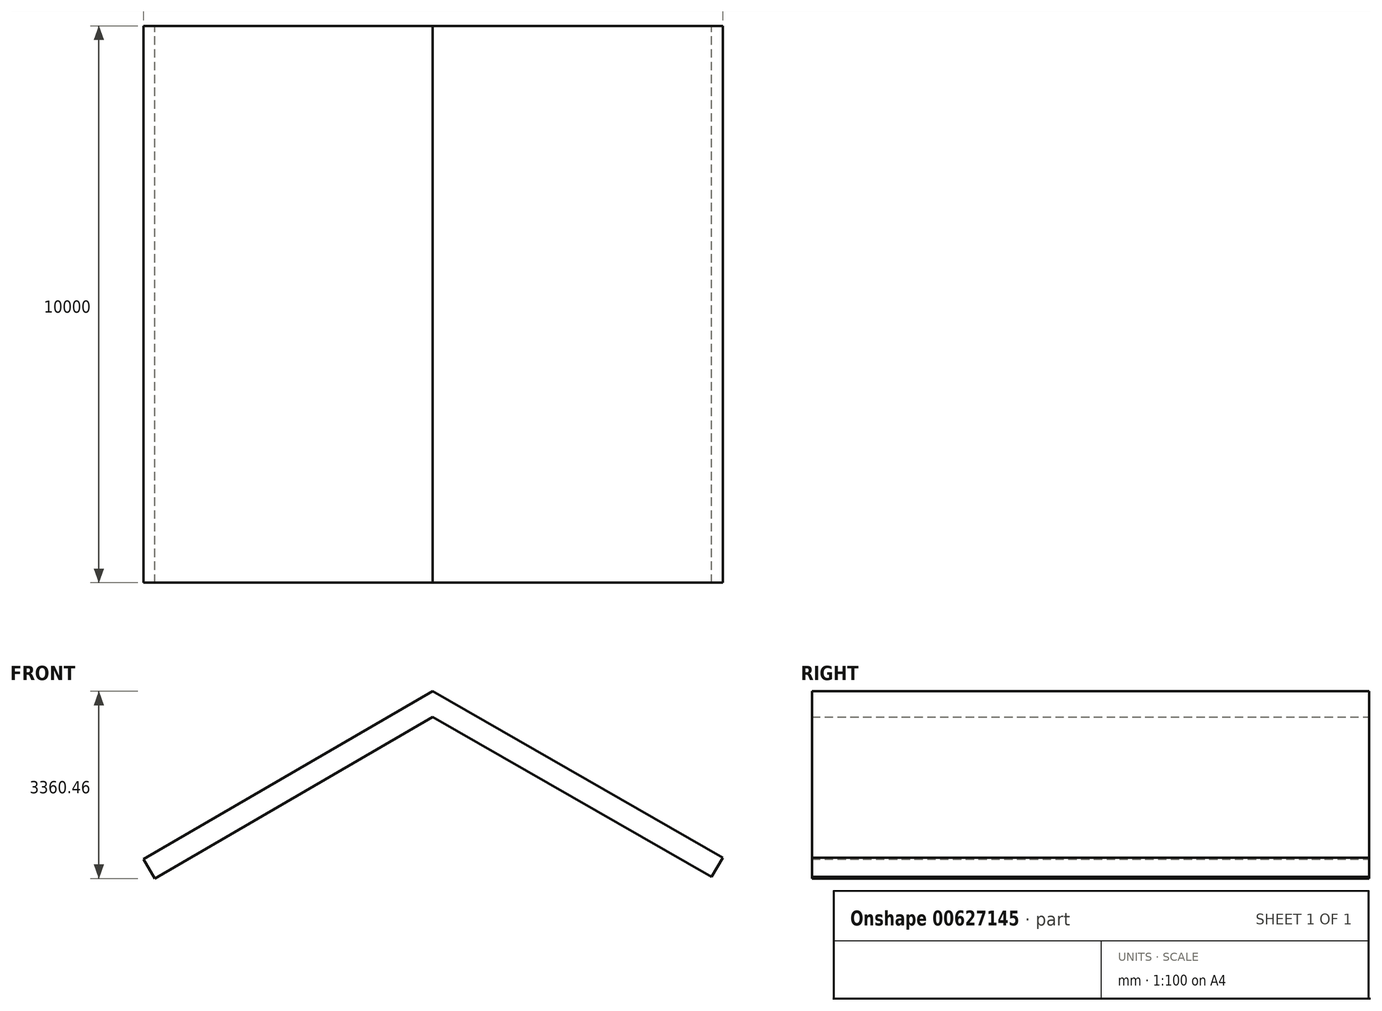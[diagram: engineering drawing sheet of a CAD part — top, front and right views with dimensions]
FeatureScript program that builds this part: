
annotation { "Feature Type Name" : "Feature", "Feature Type Description" : "" }
export const myFeature = defineFeature(function(context is Context, id is Id, definition is map)
    precondition{}
    {
        {
            var Q0;
            Q0=qCreatedBy(makeId("Front.planeOp"),FACE);
            var sketch = newSketch(context, id + "F0", { "sketchPlane" : qUnion([Q0])});
            skLineSegment(sketch, "E0", {"start": v(-86.15, -17.85) * mm, "end": v(5101.54, 2996.77) * mm});
            skLineSegment(sketch, "E1", {"start": v(5101.54, 2996.77) * mm, "end": v(10306.11, 11.4) * mm});
            skLineSegment(sketch, "E2.0", {"start": v(5102.84, 2534.89) * mm, "end": v(10107.1, -335.56) * mm});
            skLineSegment(sketch, "E2.1", {"start": v(114.82, -363.7) * mm, "end": v(5102.84, 2534.89) * mm});
            skLineSegment(sketch, "E3", {"start": v(-86.15, -17.85) * mm, "end": v(114.82, -363.7) * mm});
            skLineSegment(sketch, "E4", {"start": v(10107.1, -335.56) * mm, "end": v(10306.11, 11.4) * mm});
            skSolve(sketch);
        }
        {
            var Q0;
            Q0=makeQuery(id+"F0.imprint","IMPRINT",FACE,{"disambiguationData":[TD([[makeQuery(id+"F0.imprint","IMPRINT",EDGE,{"derivedFrom":sQuery(id+"F0.wireOp",EDGE,"E0")}),-1.0]])]});
            extrude(context, id + "F1", {"entities" : qUnion([Q0]), "depth" : 10000 * mm, "offsetDistance" : 25 * mm});
        }
    });
